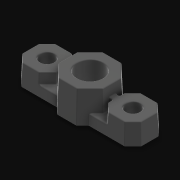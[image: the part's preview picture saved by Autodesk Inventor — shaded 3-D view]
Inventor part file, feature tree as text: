
AUTODESK INVENTOR PART (.ipt)
format: ipt  version: 2021 (Build 250183000, 183)  size: 932,352 bytes
history: native  units: in
note: dims shown in document units (in); Inventor stores cm internally (conversion verified against a paired STEP export)
features: fillet x1, other x1, imported_body x1
ambient origin geometry x8: Origin, YZ Plane, XZ Plane, XY Plane, X Axis, Y Axis, Z Axis, Center Point
bodies: Body1 (feature_tree)
feature tree (3):
  fillet  "Fillet7"  [1 undecoded]
  other  "276-3521-STEP1"
  imported_body  "Base1"
note: 1 required parameter value undecoded (feature->parameter linkage not recoverable at this tier; creation-order binding heuristic only, values carry confidence <= 0.55)
